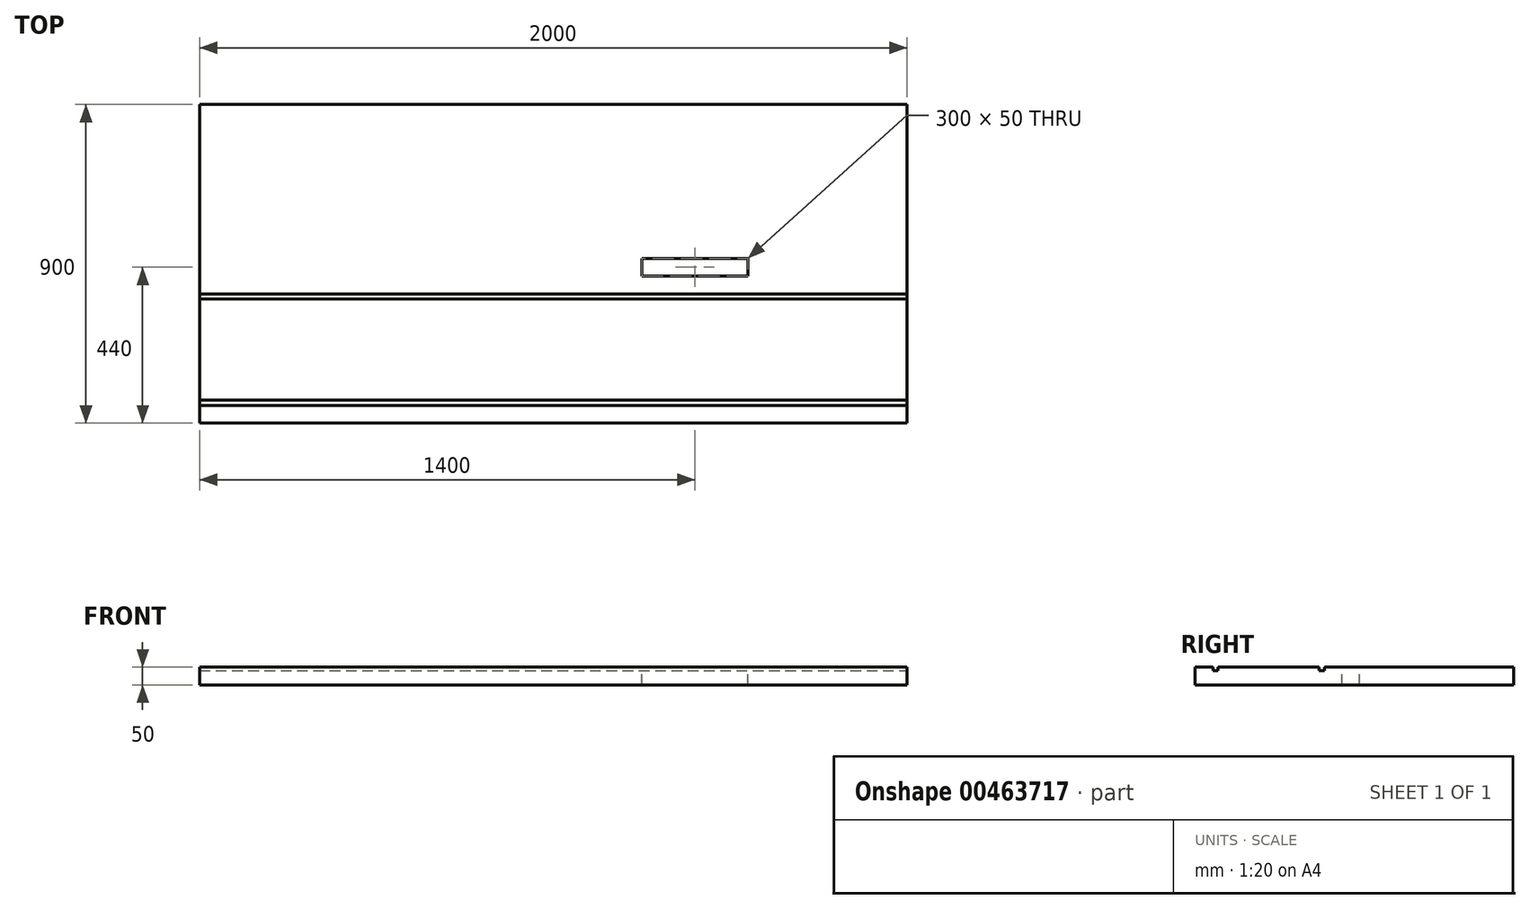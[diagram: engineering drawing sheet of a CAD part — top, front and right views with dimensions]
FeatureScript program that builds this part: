
annotation { "Feature Type Name" : "Feature", "Feature Type Description" : "" }
export const myFeature = defineFeature(function(context is Context, id is Id, definition is map)
    precondition{}
    {
        {
            var Q0;
            Q0=qCreatedBy(makeId("Top.planeOp"),FACE);
            var sketch = newSketch(context, id + "F0", { "sketchPlane" : qUnion([Q0])});
            skLineSegment(sketch, "E0.bottom", {"start": v(1000, 450) * mm, "end": v(-1000, 450) * mm});
            skLineSegment(sketch, "E0.top", {"start": v(1000, -450) * mm, "end": v(-1000, -450) * mm});
            skLineSegment(sketch, "E0.left", {"start": v(1000, 450) * mm, "end": v(1000, -450) * mm});
            skLineSegment(sketch, "E0.right", {"start": v(-1000, 450) * mm, "end": v(-1000, -450) * mm});
            skPoint(sketch, "E0.middle", {"position": v(0, 0) * mm});
            skSolve(sketch);
        }
        {
            var Q0;
            Q0=makeQuery(id+"F0.imprint","IMPRINT",FACE,{"disambiguationData":[TD([[makeQuery(id+"F0.imprint","IMPRINT",EDGE,{"derivedFrom":sQuery(id+"F0.wireOp",EDGE,"E0.bottom")}),1.0]])]});
            extrude(context, id + "F1", {"entities" : qUnion([Q0]), "depth" : 50 * mm});
        }
        {
            var Q0;
            Q0=makeQuery(id+"F1.opExtrude","SWEPT_FACE",FACE,{"disambiguationData":[OSD([sQuery(id+"F0.wireOp",EDGE,"E0.left")])]});
            var sketch = newSketch(context, id + "F2", { "sketchPlane" : qUnion([Q0])});
            skLineSegment(sketch, "E1.bottom", {"start": v(-350.07, 50) * mm, "end": v(-295.78, 50) * mm});
            skLineSegment(sketch, "E1.top", {"start": v(-350.07, 25.51) * mm, "end": v(-295.78, 25.51) * mm});
            skLineSegment(sketch, "E1.left", {"start": v(-350.07, 50) * mm, "end": v(-350.07, 25.51) * mm});
            skLineSegment(sketch, "E1.right", {"start": v(-295.78, 50) * mm, "end": v(-295.78, 25.51) * mm});
            skSolve(sketch);
        }
        {
            var Q0;
            Q0 = qSketchRegion(id + "F2", true);
            var sketch = newSketch(context, id + "F3", { "sketchPlane" : qUnion([Q0])});
            skLineSegment(sketch, "E2.bottom", {"start": v(-100, 50) * mm, "end": v(-85, 50) * mm});
            skLineSegment(sketch, "E2.top", {"start": v(-100, 40) * mm, "end": v(-85, 40) * mm});
            skLineSegment(sketch, "E2.left", {"start": v(-100, 50) * mm, "end": v(-100, 40) * mm});
            skLineSegment(sketch, "E2.right", {"start": v(-85, 50) * mm, "end": v(-85, 40) * mm});
            skSolve(sketch);
        }
        {
            var Q0;
            Q0=makeQuery(id+"F3.imprint","IMPRINT",FACE,{"disambiguationData":[TD([[makeQuery(id+"F3.imprint","IMPRINT",EDGE,{"derivedFrom":sQuery(id+"F3.wireOp",EDGE,"E2.bottom")}),-1.0]])]});
            extrude(context, id + "F4", {"entities" : qUnion([Q0]), "operationType" : NewBodyOperationType.REMOVE, "oppositeDirection" : true, "depth" : 2000 * mm});
        }
        {
            var Q0;
            Q0=makeQuery(id+"F1.opExtrude","SWEPT_FACE",FACE,{"disambiguationData":[OSD([sQuery(id+"F0.wireOp",EDGE,"E0.left")])]});
            var sketch = newSketch(context, id + "F5", { "sketchPlane" : qUnion([Q0])});
            skLineSegment(sketch, "E3.bottom", {"start": v(-400, 50) * mm, "end": v(-385, 50) * mm});
            skLineSegment(sketch, "E3.top", {"start": v(-400, 40) * mm, "end": v(-385, 40) * mm});
            skLineSegment(sketch, "E3.left", {"start": v(-400, 50) * mm, "end": v(-400, 40) * mm});
            skLineSegment(sketch, "E3.right", {"start": v(-385, 50) * mm, "end": v(-385, 40) * mm});
            skSolve(sketch);
        }
        {
            var Q0;
            Q0=makeQuery(id+"F5.imprint","IMPRINT",FACE,{"disambiguationData":[TD([[makeQuery(id+"F5.imprint","IMPRINT",EDGE,{"derivedFrom":sQuery(id+"F5.wireOp",EDGE,"E3.bottom")}),1.0]])]});
            extrude(context, id + "F6", {"entities" : qUnion([Q0]), "operationType" : NewBodyOperationType.REMOVE, "oppositeDirection" : true, "depth" : 2000 * mm});
        }
        {
            var Q0;
            {var subQ0=sQuery(id+"F0.wireOp",EDGE,"E0.bottom");var subQ1=sQuery(id+"F0.wireOp",EDGE,"E0.right");var subQ2=sQuery(id+"F0.wireOp",EDGE,"E0.left");Q0=makeQuery(id+"F4.boolean.opBoolean","SPLIT",FACE,{"disambiguationData":[TD([makeQuery(id+"F1.opExtrude","SWEPT_FACE",FACE,{"disambiguationData":[OSD([subQ0])]})])],"derivedFrom":makeQuery(id+"F1.opExtrude","CAP_FACE",FACE,{"disambiguationData":[OSD([subQ0,sQuery(id+"F0.wireOp",EDGE,"E0.top"),subQ2,subQ1])],"isStart":false})});}
            var sketch = newSketch(context, id + "F7", { "sketchPlane" : qUnion([Q0])});
            skLineSegment(sketch, "E4.bottom", {"start": v(250, 15) * mm, "end": v(550, 15) * mm});
            skLineSegment(sketch, "E4.top", {"start": v(250, -35) * mm, "end": v(550, -35) * mm});
            skLineSegment(sketch, "E4.left", {"start": v(250, 15) * mm, "end": v(250, -35) * mm});
            skLineSegment(sketch, "E4.right", {"start": v(550, 15) * mm, "end": v(550, -35) * mm});
            skSolve(sketch);
        }
        {
            var Q0;
            Q0=makeQuery(id+"F7.imprint","IMPRINT",FACE,{"disambiguationData":[TD([[makeQuery(id+"F7.imprint","IMPRINT",EDGE,{"derivedFrom":sQuery(id+"F7.wireOp",EDGE,"E4.bottom")}),-1.0]])]});
            extrude(context, id + "F8", {"entities" : qUnion([Q0]), "operationType" : NewBodyOperationType.REMOVE, "oppositeDirection" : true, "depth" : 50 * mm});
        }
    });
